# Revit family: Поли-Групп_ЗадвижкаКлиноваяEAZ-МК-F4(ВS)_DN40-600
name_source: partatom
category: Арматура трубопроводов
units: mm (PartAtom-declared; Revit-internal decimal feet)

## family parameters
Всегда вертикально = Да
На основе рабочей плоскости = Нет
Общий = Нет
При загрузке вырезать с полостями = Нет
Размер круглого соединителя = Использовать диаметр
Тип детали = Клапан - Вставляется

## types (15) — shared parameters
ADSK_URL страницы изделия = https://www.polycorr.ru
ADSK_Версия Revit = 2019
ADSK_Единица измерения = шт
ADSK_Завод-изготовитель = ООО ПК «Поли-Групп»
ADSK_Количество = 1
ADSK_Материал = Высокопрочный чугун GGG-40
ADSK_Материал наименование = Высокопрочный чугун с шаровидным графитом (GGG-40)
Kv = 1.0 м³/ч
PN = 10.0 бары
Класс герметичности = А по ГОСТ Р 9544-2015
Материал Диска = Высокопрочный чугун с шаровидным графитом (GGG-40)
Материал уплотнителя = PTFE
Назначение = Для установки в качестве запорного устройства на трубопроводах
Покрытие = Высококачественное эпоксидное покрытие толщиной 300 мкм
Рабочая среда = Техническая вода, канализационные стоки, морская вода
Разработчик = https://3dbim.pro
Срок службы = 50 лет
ТВ = Поли-Групп_ЗадвижкаКлиноваяEAZ-МК-F4(ВS)_DN40-600
Температура рабочей среды = 0 до +70°С
Тип привода = Штурвал
Тип присоединения = Фланцевое

## per-type parameters (varying)
| type | A | ADSK_Марка | ADSK_Масса | ADSK_Масса_Текст | ADSK_Наименование | ADSK_Наименование краткое | D | D2 | DN | DO | D_Наружный | H2 | L | R | b | d1 | f | h2 | l1 | l2 | l3 | t | Габаритные размеры |
| 40-10 | 135 мм | EAZ-GV-2-F4 DN40 PN10 | 10 | 10 | Задвижка клиновая с металлическим уплотнением EAZ MK F4 для сточных вод фланцевая DN40 PN10 | Задвижка клиновая EAZ MK F4 DN40 PN10 | 150 мм | 84 мм | 40 мм | 160 мм | 49 мм | 245 мм | 140 мм | 10 мм | 16 мм | 10 мм | 3 мм | 123 мм | 84 мм | 91 мм | 126 мм | 12 мм | 150х140х245 |
| 50-10 | 149 мм | EAZ-GV-2-F4 DN50 PN10 | 12 | 12 | Задвижка клиновая с металлическим уплотнением EAZ MK F4 для сточных вод фланцевая DN50 PN10 | Задвижка клиновая EAZ MK F4 DN50 PN10 | 165 мм | 99 мм | 50 мм | 160 мм | 59 мм | 255 мм | 150 мм | 10 мм | 16 мм | 13 мм | 3 мм | 128 мм | 90 мм | 98 мм | 135 мм | 13 мм | 165х150х255 |
| 65-10 | 167 мм | EAZ-GV-2-F4 DN65 PN10 | 15 | 15 | Задвижка клиновая с металлическим уплотнением EAZ MK F4 для сточных вод фланцевая DN65 PN10 | Задвижка клиновая EAZ MK F4 DN65 PN10 | 185 мм | 118 мм | 65 мм | 160 мм | 74 мм | 277 мм | 170 мм | 10 мм | 16 мм | 16 мм | 3 мм | 139 мм | 102 мм | 111 мм | 153 мм | 14 мм | 185х170х277 |
| 80-10 | 180 мм | EAZ-GV-2-F4 DN80 PN10 | 18 | 18 | Задвижка клиновая с металлическим уплотнением EAZ MK F4 для сточных вод фланцевая DN80 PN10 | Задвижка клиновая EAZ MK F4 DN80 PN10 | 200 мм | 132 мм | 80 мм | 160 мм | 89 мм | 304 мм | 180 мм | 10 мм | 17 мм | 20 мм | 3 мм | 152 мм | 108 мм | 117 мм | 162 мм | 15 мм | 200х180х304 |
| 100-10 | 198 мм | EAZ-GV-2-F4 DN100 PN10 | 24 | 24 | Задвижка клиновая с металлическим уплотнением EAZ MK F4 для сточных вод фланцевая DN100 PN10 | Задвижка клиновая EAZ MK F4 DN100 PN10 | 220 мм | 156 мм | 100 мм | 200 мм | 109 мм | 332 мм | 190 мм | 11 мм | 17 мм | 25 мм | 3 мм | 166 мм | 114 мм | 124 мм | 171 мм | 17 мм | 220х190х332 |
| 125-10 | 225 мм | EAZ-GV-2-F4 DN125 PN10 | 35 | 35 | Задвижка клиновая с металлическим уплотнением EAZ MK F4 для сточных вод фланцевая DN125 PN10 | Задвижка клиновая EAZ MK F4 DN125 PN10 | 250 мм | 184 мм | 125 мм | 200 мм | 134 мм | 388 мм | 200 мм | 11 мм | 18 мм | 31 мм | 3 мм | 194 мм | 120 мм | 130 мм | 180 мм | 19 мм | 250х200х388 |
| 150-10 | 257 мм | EAZ-GV-2-F4 DN150 PN10 | 40 | 40 | Задвижка клиновая с металлическим уплотнением EAZ MK F4 для сточных вод фланцевая DN150 PN10 | Задвижка клиновая EAZ MK F4 DN150 PN10 | 285 мм | 211 мм | 150 мм | 250 мм | 159 мм | 455 мм | 210 мм | 11 мм | 20 мм | 38 мм | 3 мм | 228 мм | 126 мм | 137 мм | 189 мм | 23 мм | 285х210х455 |
| 200-10 | 306 мм | EAZ-GV-2-F4 DN200 PN10 | 70 | 70 | Задвижка клиновая с металлическим уплотнением EAZ MK F4 для сточных вод фланцевая DN200 PN10 | Задвижка клиновая EAZ MK F4 DN200 PN10 | 340 мм | 266 мм | 200 мм | 250 мм | 209 мм | 538 мм | 230 мм | 13 мм | 21 мм | 50 мм | 3 мм | 269 мм | 138 мм | 150 мм | 207 мм | 27 мм | 340х230х538 |
| 250-10 | 365 мм | EAZ-GV-2-F4 DN250 PN10 | 108 | 108 | Задвижка клиновая с металлическим уплотнением EAZ MK F4 для сточных вод фланцевая DN250 PN10 | Задвижка клиновая EAZ MK F4 DN250 PN10 | 405 мм | 319 мм | 250 мм | 320 мм | 259 мм | 629 мм | 250 мм | 15 мм | 23 мм | 63 мм | 3 мм | 315 мм | 150 мм | 163 мм | 225 мм | 31 мм | 405х250х629 |
| 300-10 | 414 мм | EAZ-GV-2-F4 DN300  PN10 | 150 | 150 | Задвижка клиновая с металлическим уплотнением EAZ MK F4 для сточных вод фланцевая DN300 PN10 | Задвижка клиновая EAZ MK F4 DN300 PN10 | 460 мм | 370 мм | 300 мм | 320 мм | 309 мм | 730 мм | 270 мм | 17 мм | 24 мм | 75 мм | 4 мм | 365 мм | 162 мм | 176 мм | 243 мм | 37 мм | 460х270х730 |
| 350-10 | 455 мм | EAZ-GV-2-F4 DN350 PN10 | 270 | 270 | Задвижка клиновая с металлическим уплотнением EAZ MK F4 для сточных вод фланцевая DN350 PN10 | Задвижка клиновая EAZ MK F4 DN350 PN10 | 505 мм | 429 мм | 350 мм | 460 мм | 359 мм | 860 мм | 290 мм | 21 мм | 25 мм | 88 мм | 4 мм | 430 мм | 174 мм | 189 мм | 261 мм | 43 мм | 505х290х1135 |
| 400-10 | 464 мм | EAZ-GV-2-F4 DN400 PN10 | 329 | 329 | Задвижка клиновая с металлическим уплотнением EAZ MK F4 для сточных вод фланцевая DN400 PN10 | Задвижка клиновая EAZ MK F4 DN400 PN10 | 515 мм | 480 мм | 400 мм | 460 мм | 409 мм | 954 мм | 310 мм | 21 мм | 25 мм | 100 мм | 4 мм | 477 мм | 186 мм | 202 мм | 279 мм | 48 мм | 515х310х1274 |
| 450-10 | 509 мм | EAZ-GV-2-F4 DN450 PN10 | 430 | 430 | Задвижка клиновая с металлическим уплотнением EAZ MK F4 для сточных вод фланцевая DN450 PN10 | Задвижка клиновая EAZ MK F4 DN450 PN10 | 565 мм | 530 мм | 450 мм | 460 мм | 459 мм | 1039 мм | 330 мм | 28 мм | 26 мм | 113 мм | 4 мм | 520 мм | 198 мм | 215 мм | 297 мм | 52 мм | 565х330х1374 |
| 500-10 | 558 мм | EAZ-GV-2-F4 DN500 PN10 | 558 | 558 | Задвижка клиновая с металлическим уплотнением EAZ MK F4 для сточных вод фланцевая DN500 PN10 | Задвижка клиновая EAZ MK F4 DN500 PN10 | 620 мм | 582 мм | 500 мм | 640 мм | 509 мм | 1120 мм | 350 мм | 28 мм | 27 мм | 125 мм | 4 мм | 560 мм | 210 мм | 228 мм | 315 мм | 56 мм | 620х350х1510 |
| 600-10 | 653 мм | EAZ-GV-2-F4 DN600 PN10 | 714 | 714 | Задвижка клиновая с металлическим уплотнением EAZ MK F4 для сточных вод фланцевая DN600 PN10 | Задвижка клиновая EAZ MK F4 DN600 PN10 | 725 мм | 682 мм | 600 мм | 900 мм | 609 мм | 1280 мм | 390 мм | 28 мм | 30 мм | 150 мм | 5 мм | 640 мм | 234 мм | 254 мм | 351 мм | 64 мм | 725х390х1736 |
